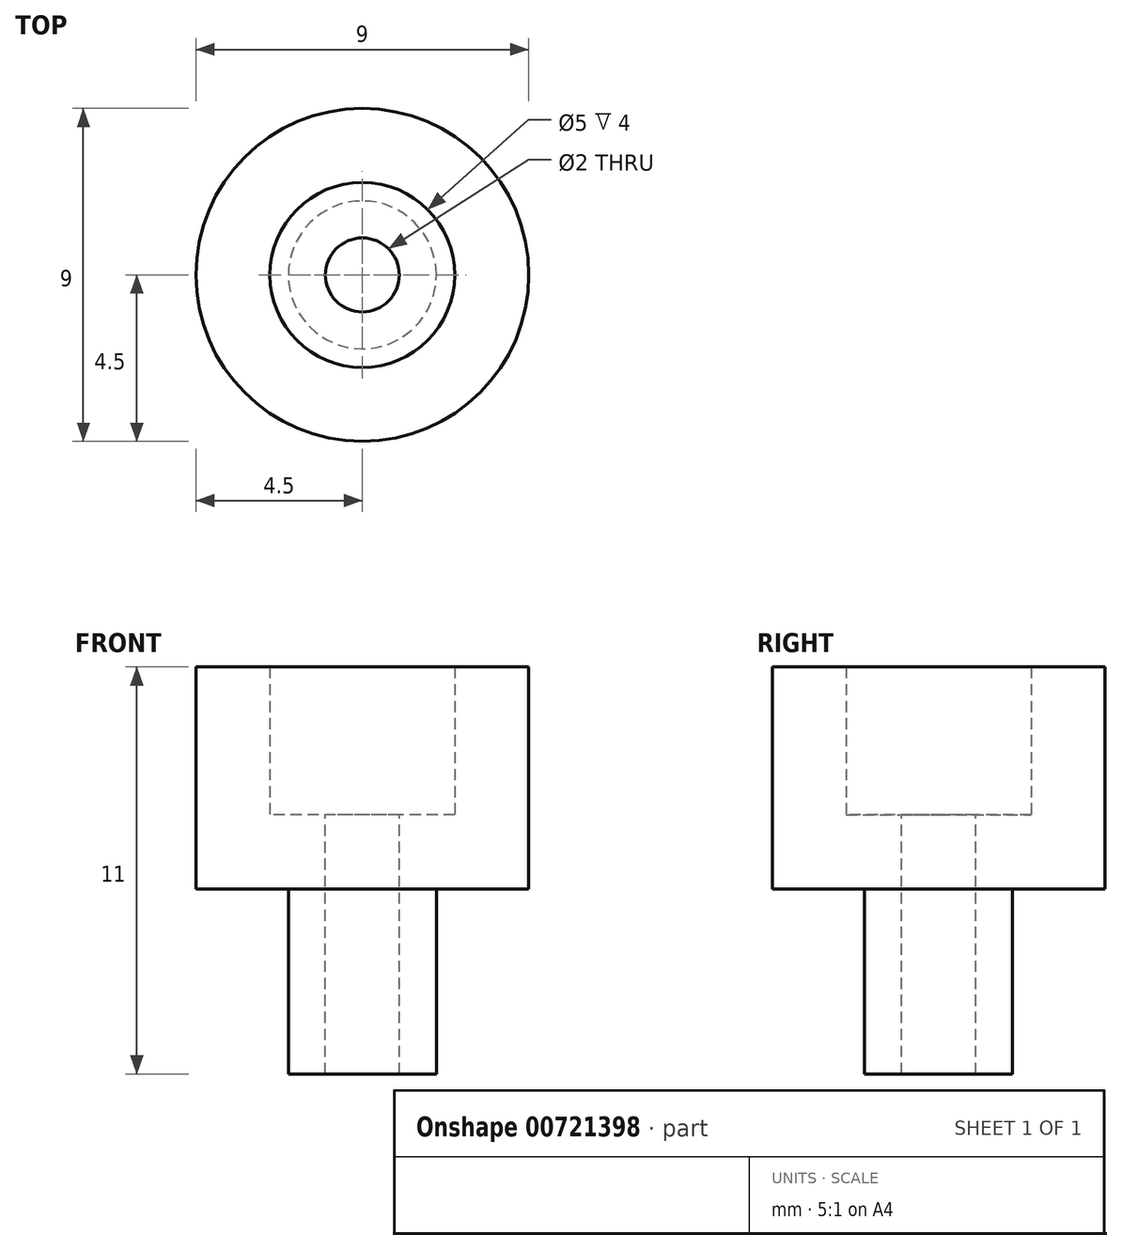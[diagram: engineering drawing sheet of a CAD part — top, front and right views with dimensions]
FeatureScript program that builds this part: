
annotation { "Feature Type Name" : "Feature", "Feature Type Description" : "" }
export const myFeature = defineFeature(function(context is Context, id is Id, definition is map)
    precondition{}
    {
        {
            var Q0;
            Q0=qCreatedBy(makeId("Top.planeOp"),FACE);
            var sketch = newSketch(context, id + "F0", { "sketchPlane" : qUnion([Q0])});
            skCircle(sketch, "E0", {"center": v(0, 0) * mm, "radius": 4.5 * mm});
            skSolve(sketch);
        }
        {
            var Q0;
            Q0=makeQuery(id+"F0.imprint","IMPRINT",FACE,{"disambiguationData":[TD([[makeQuery(id+"F0.imprint","IMPRINT",EDGE,{"derivedFrom":sQuery(id+"F0.wireOp",EDGE,"E0")}),1.0]])]});
            extrude(context, id + "F1", {"entities" : qUnion([Q0]), "depth" : 6 * mm, "offsetDistance" : 25 * mm});
        }
        {
            var Q0;
            Q0=makeQuery(id+"F1.opExtrude","CAP_FACE",FACE,{"disambiguationData":[OSD([sQuery(id+"F0.wireOp",EDGE,"E0")])],"isStart":false});
            shell(context, id + "F2", {"entities" : qUnion([Q0]), "thickness" : 2 * mm});
        }
        {
            var Q0;
            Q0=makeQuery(id+"F1.opExtrude","CAP_FACE",FACE,{"disambiguationData":[OSD([sQuery(id+"F0.wireOp",EDGE,"E0")])],"isStart":true});
            var sketch = newSketch(context, id + "F3", { "sketchPlane" : qUnion([Q0])});
            skCircle(sketch, "E1", {"center": v(0, 0) * mm, "radius": 2 * mm});
            skSolve(sketch);
        }
        {
            var Q0;
            Q0=makeQuery(id+"F3.imprint","IMPRINT",FACE,{"disambiguationData":[TD([[makeQuery(id+"F3.imprint","IMPRINT",EDGE,{"derivedFrom":sQuery(id+"F3.wireOp",EDGE,"E1")}),1.0]])]});
            extrude(context, id + "F4", {"entities" : qUnion([Q0]), "operationType" : NewBodyOperationType.ADD, "depth" : 5 * mm, "offsetDistance" : 25 * mm});
        }
        {
            var Q0;
            Q0=makeQuery(id+"F4.opExtrude","CAP_FACE",FACE,{"disambiguationData":[OSD([sQuery(id+"F3.wireOp",EDGE,"E1")])],"isStart":false});
            shell(context, id + "F5", {"entities" : qUnion([Q0]), "thickness" : 1 * mm});
        }
        {
            var Q0;
            Q0=makeQuery(id+"F1.opExtrude","CAP_FACE",FACE,{"disambiguationData":[OSD([sQuery(id+"F0.wireOp",EDGE,"E0")])],"isStart":true});
            var sketch = newSketch(context, id + "F6", { "sketchPlane" : qUnion([Q0])});
            skCircle(sketch, "E2", {"center": v(0, 0) * mm, "radius": 1 * mm});
            skSolve(sketch);
        }
        {
            var Q0;
            Q0=makeQuery(id+"F6.imprint","IMPRINT",FACE,{"disambiguationData":[TD([[makeQuery(id+"F6.imprint","IMPRINT",EDGE,{"derivedFrom":sQuery(id+"F6.wireOp",EDGE,"E2")}),1.0]])]});
            extrude(context, id + "F7", {"entities" : qUnion([Q0]), "operationType" : NewBodyOperationType.REMOVE, "endBound" : BoundingType.SYMMETRIC, "oppositeDirection" : true, "depth" : 25 * mm, "offsetDistance" : 25 * mm});
        }
    });
